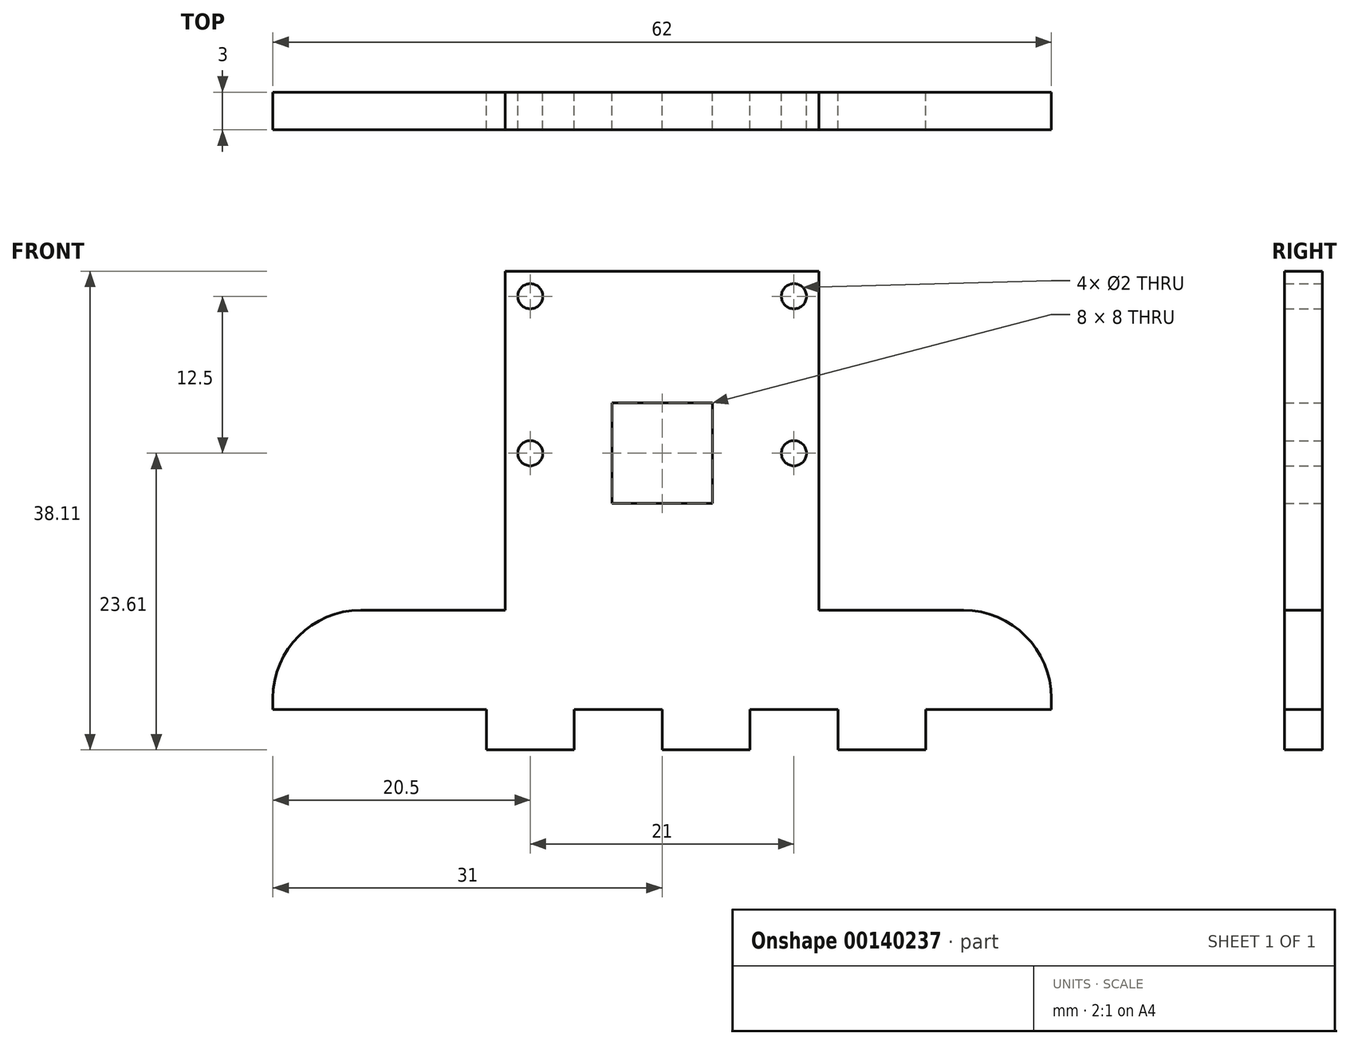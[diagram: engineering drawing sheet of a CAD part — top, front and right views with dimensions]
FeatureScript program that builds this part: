
annotation { "Feature Type Name" : "Feature", "Feature Type Description" : "" }
export const myFeature = defineFeature(function(context is Context, id is Id, definition is map)
    precondition{}
    {
        {
            var Q0;
            Q0=qCreatedBy(makeId("Front.planeOp"),FACE);
            var sketch = newSketch(context, id + "F0", { "sketchPlane" : qUnion([Q0])});
            skLineSegment(sketch, "E0.bottom", {"start": v(12.5, 13.5) * mm, "end": v(-12.5, 13.5) * mm});
            skLineSegment(sketch, "E0.left", {"start": v(12.5, 13.5) * mm, "end": v(12.5, -13.5) * mm});
            skLineSegment(sketch, "E0.right", {"start": v(-12.5, 13.5) * mm, "end": v(-12.5, -13.5) * mm});
            skPoint(sketch, "E0.middle", {"position": v(0, 0) * mm});
            skLineSegment(sketch, "E1", {"start": v(0, 13.5) * mm, "end": v(0, -1) * mm, "construction": true});
            skPoint(sketch, "E1.endSnap0", {"position": v(0, 13.5) * mm});
            skLineSegment(sketch, "E2.bottom", {"start": v(4, 3) * mm, "end": v(-4, 3) * mm});
            skLineSegment(sketch, "E2.top", {"start": v(4, -5) * mm, "end": v(-4, -5) * mm});
            skLineSegment(sketch, "E2.left", {"start": v(4, 3) * mm, "end": v(4, -5) * mm});
            skLineSegment(sketch, "E2.right", {"start": v(-4, 3) * mm, "end": v(-4, -5) * mm});
            skPoint(sketch, "E2.middle", {"position": v(0, -1) * mm});
            skCircle(sketch, "E3", {"center": v(-10.5, 11.5) * mm, "radius": 1 * mm});
            skCircle(sketch, "E4", {"center": v(-10.5, -1) * mm, "radius": 1 * mm});
            skPoint(sketch, "E4.centerSnap0", {"position": v(-4, -1) * mm});
            skCircle(sketch, "E5.MirrorC", {"center": v(10.5, 11.5) * mm, "radius": 1 * mm});
            skCircle(sketch, "E6.MirrorC", {"center": v(10.5, -1) * mm, "radius": 1 * mm});
            skPoint(sketch, "E7.MirrorCS.start.orphan", {"position": v(0, -19.95) * mm});
            skLineSegment(sketch, "E8", {"start": v(-28, -19.61) * mm, "end": v(28, -19.61) * mm, "construction": true});
            skLineSegment(sketch, "E9", {"start": v(31, -21.41) * mm, "end": v(31, -19.51) * mm, "construction": true});
            skLineSegment(sketch, "E10", {"start": v(-31, -21.41) * mm, "end": v(-31, -19.51) * mm});
            skLineSegment(sketch, "E11", {"start": v(31, -19.51) * mm, "end": v(31, -21.41) * mm});
            skLineSegment(sketch, "E12", {"start": v(-31, -21.41) * mm, "end": v(-14, -21.41) * mm});
            skLineSegment(sketch, "E13", {"start": v(-14, -21.41) * mm, "end": v(-14, -24.61) * mm});
            skLineSegment(sketch, "E14", {"start": v(-14, -24.61) * mm, "end": v(-7, -24.61) * mm});
            skLineSegment(sketch, "E15", {"start": v(-7, -24.61) * mm, "end": v(-7, -21.41) * mm});
            skLineSegment(sketch, "E16", {"start": v(-7, -21.41) * mm, "end": v(0, -21.41) * mm});
            skLineSegment(sketch, "E17", {"start": v(0, -21.41) * mm, "end": v(0, -24.61) * mm});
            skLineSegment(sketch, "E18", {"start": v(0, -24.61) * mm, "end": v(7, -24.61) * mm});
            skLineSegment(sketch, "E19", {"start": v(7, -24.61) * mm, "end": v(7, -21.41) * mm});
            skLineSegment(sketch, "E20", {"start": v(7, -21.41) * mm, "end": v(14, -21.41) * mm});
            skLineSegment(sketch, "E21", {"start": v(14, -21.41) * mm, "end": v(14, -24.61) * mm});
            skLineSegment(sketch, "E22", {"start": v(14, -24.61) * mm, "end": v(21, -24.61) * mm});
            skLineSegment(sketch, "E23", {"start": v(21, -24.61) * mm, "end": v(21, -21.41) * mm});
            skLineSegment(sketch, "E24", {"start": v(21, -21.41) * mm, "end": v(31, -21.41) * mm});
            skLineSegment(sketch, "E25", {"start": v(0, -13.5) * mm, "end": v(-43.73, -13.5) * mm, "construction": true});
            skLineSegment(sketch, "E26", {"start": v(0, -13.5) * mm, "end": v(36.07, -13.5) * mm, "construction": true});
            skLineSegment(sketch, "E27", {"start": v(-31, -20.5) * mm, "end": v(-31, -19.51) * mm});
            skLineSegment(sketch, "E28", {"start": v(-24, -13.5) * mm, "end": v(-12.5, -13.5) * mm});
            skLineSegment(sketch, "E29", {"start": v(12.5, -13.5) * mm, "end": v(24, -13.5) * mm});
            skLineSegment(sketch, "E30", {"start": v(31, -19.51) * mm, "end": v(31, -20.5) * mm});
            skPoint(sketch, "E31.visualSharp", {"position": v(-31, -13.5) * mm});
            skArc(sketch, "E31.filletArc", {"start": v(-24, -13.5) * mm, "mid": v(-28.95, -15.55) * mm, "end": v(-31, -20.5) * mm});
            skPoint(sketch, "E32.visualSharp", {"position": v(31, -13.5) * mm});
            skArc(sketch, "E32.filletArc", {"start": v(31, -20.5) * mm, "mid": v(28.95, -15.55) * mm, "end": v(24, -13.5) * mm});
            skSolve(sketch);
        }
        {
            var Q0;
            Q0=qSketchRegion(id+"F0",true);
            extrude(context, id + "F1", {"entities" : qUnion([Q0]), "endBound" : BoundingType.SYMMETRIC, "depth" : 3 * mm});
        }
    });
